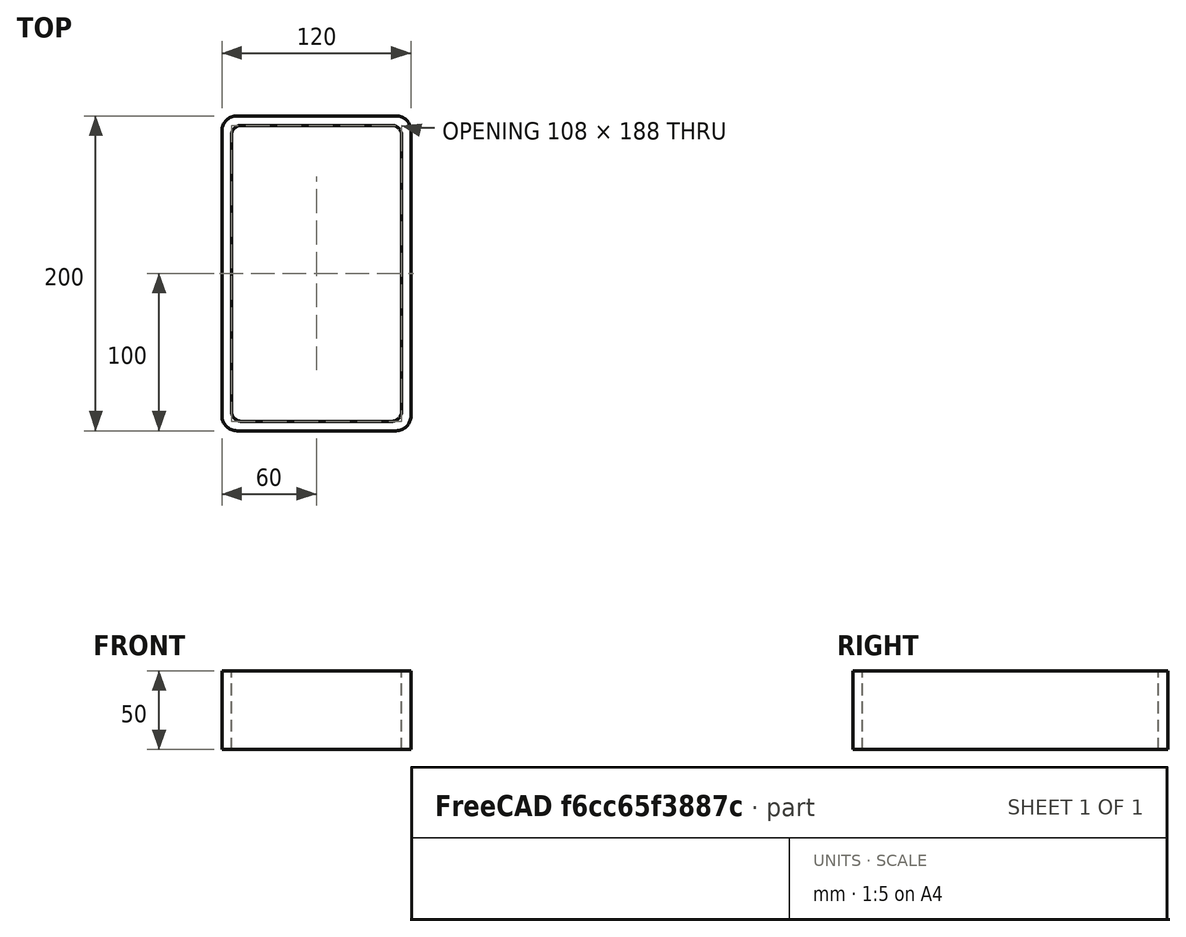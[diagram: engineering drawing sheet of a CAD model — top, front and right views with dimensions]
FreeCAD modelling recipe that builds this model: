
FCSTD DOCUMENT  (FreeCAD 0.15R4671 (Git))
Label: Rectangular hollow section 200x120x6 EN10219 S235JRH
License: All rights reserved
LicenseURL: http://en.wikipedia.org/wiki/All_rights_reserved
objects: Sketcher::SketchObject×1, Part::Extrusion×1
note: 2 computed .brp shape members not serialized (recipe doc carries the construction recipe); baked Part::Feature solids carry a one-line shape summary decoded from their .brp

FEATURE [Sketcher::SketchObject] Sketch
  sketch-geometry (16):
    g0: LineSegment StartX=-47.7 StartY=94 StartZ=0 EndX=47.7 EndY=94 EndZ=0
    g1: LineSegment StartX=54 StartY=87.7 StartZ=0 EndX=54 EndY=-87.7 EndZ=0
    g2: LineSegment StartX=47.7 StartY=-94 StartZ=0 EndX=-47.7 EndY=-94 EndZ=0
    g3: LineSegment StartX=-54 StartY=-87.7 StartZ=0 EndX=-54 EndY=87.7 EndZ=0
    g4: LineSegment StartX=-50.55 StartY=100 StartZ=0 EndX=50.55 EndY=100 EndZ=0
    g5: LineSegment StartX=60 StartY=90.55 StartZ=0 EndX=60 EndY=-90.55 EndZ=0
    g6: LineSegment StartX=50.55 StartY=-100 StartZ=0 EndX=-50.55 EndY=-100 EndZ=0
    g7: LineSegment StartX=-60 StartY=-90.55 StartZ=0 EndX=-60 EndY=90.55 EndZ=0
    g8: ArcOfCircle CenterX=-47.7 CenterY=87.7 CenterZ=0 NormalX=0 NormalY=0 NormalZ=1 Radius=6.3 StartAngle=1.5708 EndAngle=3.14159
    g9: ArcOfCircle CenterX=47.7 CenterY=87.7 CenterZ=0 NormalX=0 NormalY=0 NormalZ=1 Radius=6.3 StartAngle=0 EndAngle=1.5708
    g10: ArcOfCircle CenterX=47.7 CenterY=-87.7 CenterZ=0 NormalX=0 NormalY=0 NormalZ=1 Radius=6.3 StartAngle=4.71239 EndAngle=6.28319
    g11: ArcOfCircle CenterX=-47.7 CenterY=-87.7 CenterZ=0 NormalX=0 NormalY=0 NormalZ=1 Radius=6.3 StartAngle=3.14159 EndAngle=4.71239
    g12: ArcOfCircle CenterX=50.55 CenterY=90.55 CenterZ=0 NormalX=0 NormalY=0 NormalZ=1 Radius=9.45 StartAngle=0 EndAngle=1.5708
    g13: ArcOfCircle CenterX=50.55 CenterY=-90.55 CenterZ=0 NormalX=0 NormalY=0 NormalZ=1 Radius=9.45 StartAngle=4.71239 EndAngle=6.28319
    g14: ArcOfCircle CenterX=-50.55 CenterY=-90.55 CenterZ=0 NormalX=0 NormalY=0 NormalZ=1 Radius=9.45 StartAngle=3.14159 EndAngle=4.71239
    g15: ArcOfCircle CenterX=-50.55 CenterY=90.55 CenterZ=0 NormalX=0 NormalY=0 NormalZ=1 Radius=9.45 StartAngle=1.5708 EndAngle=3.14159
  constraints (36):
    c: Horizontal(g2)
    c: Vertical(g3)
    c: Horizontal(g6)
    c: Vertical(g7)
    c: Tangent(g3,g8) = 1.5708
    c: Tangent(g0,g8) = 1.5708
    c: Tangent(g0,g9) = 1.5708
    c: Tangent(g1,g9) = 1.5708
    c: Tangent(g1,g10) = 1.5708
    c: Tangent(g2,g10) = 1.5708
    c: Tangent(g2,g11) = 1.5708
    c: Tangent(g3,g11) = 1.5708
    c: Tangent(g4,g12) = 1.5708
    c: Tangent(g5,g12) = 1.5708
    c: Tangent(g5,g13) = 1.5708
    c: Tangent(g6,g13) = 1.5708
    c: Tangent(g6,g14) = 1.5708
    c: Tangent(g7,g14) = 1.5708
    c: Tangent(g7,g15) = 1.5708
    c: Tangent(g4,g15) = 1.5708
    c: Equal(g9,g8)
    c: Equal(g9,g11)
    c: Equal(g9,g10)
    c: Equal(g12,g15)
    c: Equal(g12,g14)
    c: Equal(g12,g13)
    c: Symmetric(g4,g6,g-1)
    c: Symmetric(g7,g5,g-2)
    c: DistanceY(g4,g6) = -200
    c: DistanceX(g7,g5) = 120
    c: Symmetric(g3,g1,g-2)
    c: Symmetric(g0,g2,g-1)
    c: DistanceY(g0,g4) = 6
    c: DistanceX(g5,g1) = -6
    c: Radius(g9) = 6.3
    c: Radius(g12) = 9.45
FEATURE [Part::Extrusion] Extrude  label="Rectangular hollow section 200x120x6 EN10219 S235JRH"
  Base = -> Sketch
  Dir = (0,0,50)
  Solid = true
